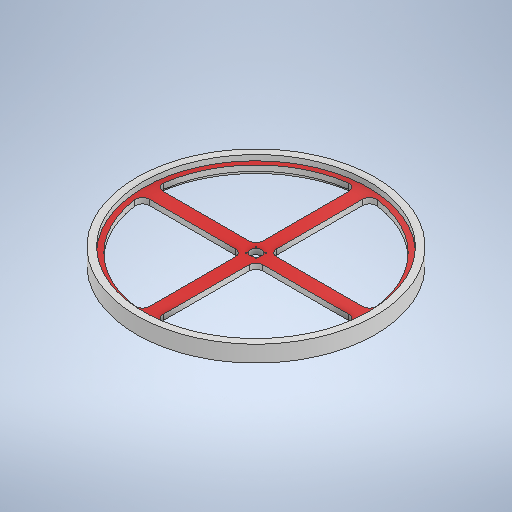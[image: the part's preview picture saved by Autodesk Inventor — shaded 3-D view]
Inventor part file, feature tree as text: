
AUTODESK INVENTOR PART (.ipt)
format: ipt  version: 2025.1 (Build 291241000, 241)  size: 346,624 bytes
history: native  units: mm
features: extrude x4, sketch x4, pattern_circular x2, plane x1, mirror x1, fillet x1, hole x1
ambient origin geometry x8: Origin, YZ Plane, XZ Plane, XY Plane, X Axis, Y Axis, Z Axis, Center Point
bodies: Solid1 (feature_tree)
feature tree (14):
  extrude  "Extrusion1"  Depth=24.0mm TaperAngle=0.0deg
  extrude  "Extrusion2"  Depth=8.0mm TaperAngle=0.0deg
  plane  "Work Plane1"
  mirror  "Mirror1"
  sketch  "Sketch3"  dims[d6=0.0mm d7=16.0mm d8=20.0mm d9=157.5mm]
  extrude  "Extrusion3"  Depth=16.0mm
  pattern_circular  "Circular Pattern1"  Count=2  [1 undecoded]
  fillet  "Fillet1"  Radius=157.5mm
  extrude  "Extrusion4"  Depth=8.0mm TaperAngle=0.0deg
  hole  "Hole1"  [1 undecoded]
  pattern_circular  "Circular Pattern2"  [2 undecoded]
  sketch  "Sketch1"  dims[d0=350.0mm d1=24.0mm d2=0.0mm]
  sketch  "Sketch2"  dims[d3=330.0mm d4=8.0mm d5=0.0mm]
  sketch  "Sketch4"  dims[d10=10.0mm d13=8.0mm d14=0.0mm d15=20.0mm d16=360.0deg d18=10.0mm d19=8.0mm d20=0.0mm d21=20.0mm d22=45.0deg d23=2.0mm d24=6.0mm d25=4.0mm d26=2.0mm d27=90.0deg d28=8.0mm d29=0.0mm d30=40.0mm d31=360.0deg]
note: 4 required parameter values undecoded (feature->parameter linkage not recoverable at this tier; creation-order binding heuristic only, values carry confidence <= 0.55)
